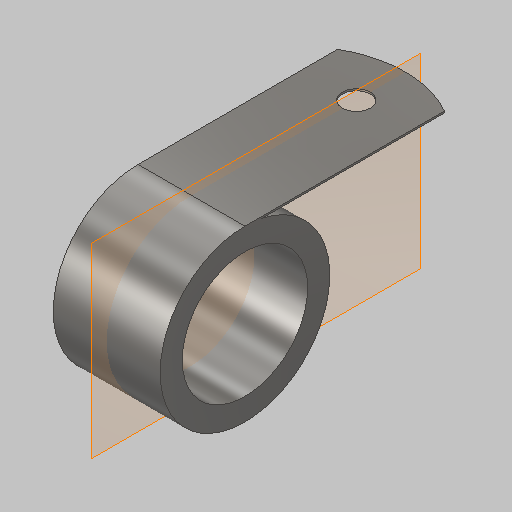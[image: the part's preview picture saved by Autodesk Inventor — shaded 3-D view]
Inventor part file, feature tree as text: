
AUTODESK INVENTOR PART (.ipt)
format: ipt  version: 2023.5 (Build 275446000, 446)  size: 138,752 bytes
history: native  units: in
note: dims shown in document units (in); Inventor stores cm internally (conversion verified against a paired STEP export)
features: plane x1, other x1
ambient origin geometry x8: Origin, YZ Plane, XZ Plane, XY Plane, X Axis, Y Axis, Z Axis, Center Point
bodies: Solid1 (feature_tree)
feature tree (2):
  plane  "Work Plane1"
  other  "OneHole"
